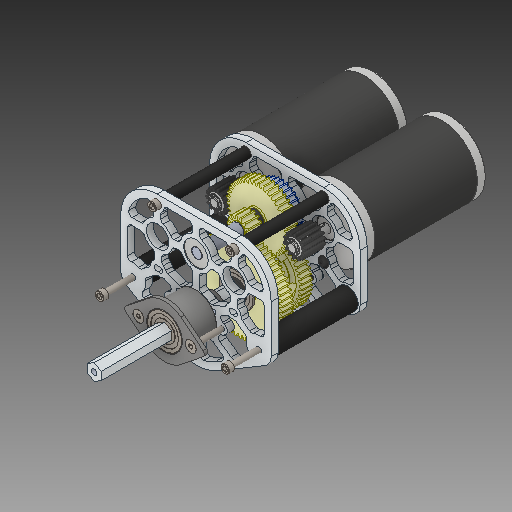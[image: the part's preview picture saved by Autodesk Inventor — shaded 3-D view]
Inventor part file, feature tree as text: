
AUTODESK INVENTOR PART (.ipt)
format: ipt  version: 2017 (Build 210142000, 142)  size: 8,169,472 bytes
history: native  units: in
note: dims shown in document units (in); Inventor stores cm internally (conversion verified against a paired STEP export)
features: other x64, move_body x2, direct_edit x1, extrude x1, sketch x1, reference x1
ambient origin geometry x8: Origin, YZ Plane, XZ Plane, XY Plane, X Axis, Y Axis, Z Axis, Center Point
bodies: Solid1 (feature_tree), Solid2 (feature_tree), Solid3 (feature_tree), Solid4 (feature_tree), Solid5 (feature_tree), Solid6 (feature_tree), Solid7 (feature_tree), Solid8 (feature_tree), Solid9 (feature_tree), Solid10 (feature_tree), Solid11 (feature_tree), Solid12 (feature_tree), Solid13 (feature_tree), Solid14 (feature_tree), Solid15 (feature_tree), Solid16 (feature_tree), Solid17 (feature_tree), Solid18 (feature_tree), Solid19 (feature_tree), Solid20 (feature_tree), Solid21 (feature_tree), Solid22 (feature_tree), Solid23 (feature_tree), Solid24 (feature_tree), Solid25 (feature_tree), Solid26 (feature_tree), Solid27 (feature_tree), Solid28 (feature_tree), Solid29 (feature_tree), Solid30 (feature_tree), Solid31 (feature_tree), Solid32 (feature_tree), Solid33 (feature_tree), Solid34 (feature_tree), Solid35 (feature_tree), Solid36 (feature_tree), Solid37 (feature_tree), Solid38 (feature_tree), Solid39 (feature_tree), Solid40 (feature_tree), Solid41 (feature_tree), Solid42 (feature_tree), Solid43 (feature_tree), Solid44 (feature_tree), Solid45 (feature_tree), Solid46 (feature_tree), Solid47 (feature_tree), Solid48 (feature_tree), Solid49 (feature_tree), Solid50 (feature_tree), Solid51 (feature_tree), Solid52 (feature_tree), Solid53 (feature_tree), Solid54 (feature_tree), Solid55 (feature_tree), Solid56 (feature_tree), Solid57 (feature_tree), Solid58 (feature_tree), Solid59 (feature_tree), Solid60 (feature_tree), Solid61 (feature_tree), Solid62 (feature_tree), Solid63 (feature_tree), Solid64 (feature_tree), Solid65 (feature_tree), Solid66 (feature_tree), Solid67 (feature_tree), Solid68 (feature_tree), Solid69 (feature_tree), Solid70 (feature_tree), Solid71 (feature_tree), Solid72 (feature_tree)
feature tree (70):
  direct_edit  "Direct Edit1"
  extrude  "Extrusion1"  Depth=1.0in TaperAngle=0.0deg
  sketch  "Sketch1"  dims[d0=0.0in d1=0.0in d2=0.9in d3=0.0in d4=0.0in d5=0.9in d6=1.0in d7=0.0in]
  reference  "Reference1"
  other  "217-3423-005 Rev1_1:1"
  other  "217-3423-006 Rev1_2:1"
  other  "217-3423-006 Rev1_3:1"
  other  "217-3423-008 Rev1_4:1"
  other  "217-3423-009 Rev3_5:1"
  other  "217-2428-027 Rev1_97414A630_6:1"
  other  "217-3195-010 Rev1_66:1"
  other  "217-3195-010 Rev1_67:1"
  other  "217-2778-NCQ8A075-050M_1032_Nut_90545A111_68:1"
  other  "91251A107_91251A107_69:1"
  other  "91251A107_91251A107_70:1"
  other  "217-2778-NCQ8A075-050M_NCQ8 Tube_075A_63:1"
  other  "217-2778-NCQ8A075-050M_NCQ8 Rod_075M_64:1"
  other  "217-2778-NCQ8A075-050M_Snap Ring_075_65:1"
  other  "217-3421-007 Rev1_16:1"
  other  "217-3421-007 Rev1_17:1"
  other  "217-3421-009 Rev1_18:1"
  other  "217-3421-009 Rev1_19:1"
  other  "217-3421-010 Rev1_20:1"
  other  "217-3421-010 Rev1_20:2"
  other  "217-3421-010 Rev1_21:1"
  other  "217-3421-010 Rev1_21:2"
  other  "217-3421-011 Rev2_97633A200_22:1"
  other  "217-3422-007 Rev1_23:1"
  other  "217-3422-007 Rev1_24:1"
  other  "217-3423-014 Rev1_25:1"
  other  "217-3423-016 Rev1_26:1"
  other  "217-3423-016 Rev1_27:1"
  other  "217-3423-016 Rev1_28:1"
  other  "217-3424-003 Rev1_29:1"
  other  "217-3424-003 Rev1_30:1"
  other  "217-3424-004 Rev1_31:1"
  other  "217-3424-004 Rev1_32:1"
  other  "217-2614-002_98430A132_33:1"
  other  "217-2614-002_98430A132_34:1"
  other  "217-2614-002_98430A132_35:1"
  other  "217-2614-002_98430A132_36:1"
  other  "217-2761-001 rev1_37:1"
  other  "217-2761-001 rev1_38:1"
  other  "217-3210-001 Rev1_30t_39:1"
  other  "217-3215-001 Rev1_42t_40:1"
  other  "217-3414-001 Rev1_14t Steel Pinion_41:1"
  other  "217-3414-001 Rev1_14t Steel Pinion_42:1"
  other  "217-3418-001 Rev2_44t_43:1"
  other  "217-3420-001 Rev2_60t_44:1"
  other  "217-3100-001_14t_45:1"
  other  "217-3423-001 Rev1_Default_As Machined__48:1"
  other  "217-3423-001 Rev1_Default_As Machined__49:1"
  other  "217-3424-005 Rev1_50:1"
  other  "217-3423-003 Rev1_51:1"
  other  "217-3423-004 Rev1_52:1"
  other  "217-3424-001 Rev1_53:1"
  other  "217-3424-001 Rev1_54:1"
  other  "217-3424-002 Rev1_55:1"
  other  "217-3424-002 Rev1_56:1"
  other  "217-3256-001 Rev1_57:1"
  other  "217-3257-001 Rev1_58:1"
  other  "217-2758-001 Rev1_59:1"
  other  "217-3259-001 Rev1_60:1"
  other  "217-3263-001 Rev1_61:1"
  other  "217-3422-004 Rev2_62:1"
  move_body  "Move1"
  move_body  "Move2"
  other  "<userpath>\Documents\GitHub\2898-STEAMworks-CAD\2898-17-A-0100\SideFrame.iam"
  other  "SideFrame.iam"
  other  "Colson_Wheel_4x2:2"
